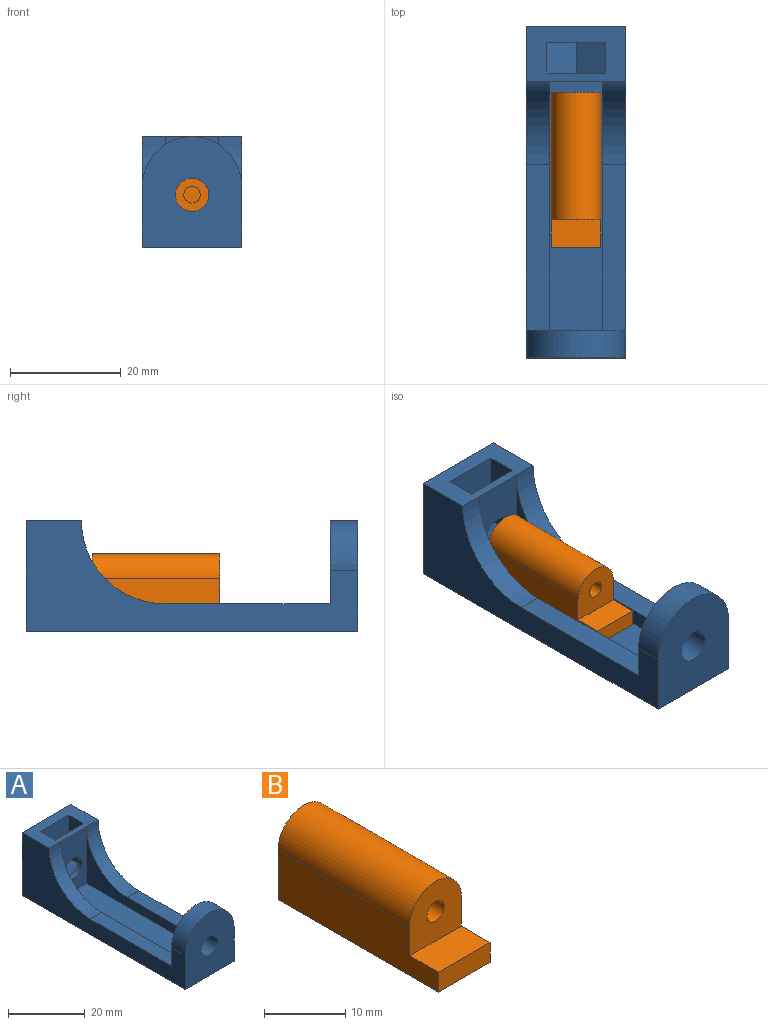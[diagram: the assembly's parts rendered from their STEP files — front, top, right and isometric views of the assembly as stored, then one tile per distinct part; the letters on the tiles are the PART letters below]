
ASSEMBLY  parts=2 mates=1
PART A: 25 faces, bbox 18x60x20 mm
  f0: plane 30x4.25mm, normal (0,0,1), area 127.5mm2, adj f3,f10,f19,f23
  f1: plane 18x10mm, normal (0,0,1), area 122.2mm2, adj f3,f4,f6,f8,f12,f13,f14,f15
  f2: cylinder r=3.25mm len=6.5mm, axis (0,1,0), area 30.6mm2, adj f8,f12
  f3: plane 60x20mm, normal (-1,0,0), area 528.3mm2, adj f0,f1,f4,f5,f7,f10,f22,f23
  f4: plane 20x18mm, normal (0,1,0), area 326.8mm2, adj f1,f3,f6,f7,f11
  f5: plane 20x18mm, normal (0,-1,0), area 297mm2, adj f3,f6,f7,f21,f22
  f6: plane 60x20mm, normal (1,0,0), area 528.3mm2, adj f1,f4,f5,f7,f9,f10,f22,f24
  f7: plane 60x18mm, normal (0,0,-1), area 1080mm2, adj f3,f4,f5,f6
  f8: plane 18x9.5mm, normal (0,-1,0), area 137.8mm2, adj f1,f2,f18,f19,f20
  f9: plane 30x4.25mm, normal (0,0,1), area 127.5mm2, adj f6,f10,f18,f24
  f10: plane 18x18mm, normal (0,1,0), area 235.5mm2, adj f0,f3,f6,f9,f18,f19,f20,f21
  f11: cylinder r=3.25mm len=6.5mm, axis (0,1,0), area 61.3mm2, adj f4,f13
  f12: plane 16.81x10.5mm, normal (0,1,0), area 127.4mm2, adj f1,f2,f14,f15,f16,f17
  f13: plane 16.81x10.5mm, normal (0,-1,0), area 127.4mm2, adj f1,f11,f14,f15,f16,f17
  f14: plane 13.78x5.5mm, normal (1,0,0), area 75.8mm2, adj f1,f12,f13,f17
  f15: plane 13.78x5.5mm, normal (-1,0,0), area 75.8mm2, adj f1,f12,f13,f16
  f16: plane 5.5x5.25mm, normal (-0.5,0,0.87), area 33.3mm2, adj f12,f13,f15,f17
  f17: plane 5.5x5.25mm, normal (0.5,0,0.87), area 33.3mm2, adj f12,f13,f14,f16
  f18: plane 45x18mm, normal (-1,0,0), area 183.3mm2, adj f8,f9,f10,f20,f24
  f19: plane 45x18mm, normal (1,0,0), area 183.3mm2, adj f0,f8,f10,f20,f23
  f20: plane 45x9.5mm, normal (0,0,1), area 427.5mm2, adj f8,f10,f18,f19
  f21: cylinder r=3mm len=6mm, axis (0,-1,0), area 94.2mm2, adj f5,f10
  f22: cylinder r=9mm len=18mm, axis (0,-1,0), area 141.4mm2, adj f3,f5,f6,f10
  f23: cylinder r=15mm len=15mm, axis (1,0,0), area 100.1mm2, adj f0,f1,f3,f19
  f24: cylinder r=15mm len=15mm, axis (1,0,0), area 100.1mm2, adj f1,f6,f9,f18
PART B: 10 faces, bbox 9x28x12 mm
  f0: plane 28x7.5mm, normal (-1,0,0), area 187.5mm2, adj f1,f3,f4,f5,f6,f9
  f1: plane 28x9mm, normal (0,0,-1), area 252mm2, adj f0,f2,f3,f4
  f2: plane 28x7.5mm, normal (1,0,0), area 187.5mm2, adj f1,f3,f4,f5,f6,f9
  f3: plane 12x9mm, normal (0,1,0), area 99.3mm2, adj f0,f1,f2,f9
  f4: plane 9x3mm, normal (0,-1,0), area 27mm2, adj f0,f1,f2,f5
  f5: plane 9x5mm, normal (0,0,1), area 45mm2, adj f0,f2,f4,f6
  f6: plane 9x9mm, normal (0,-1,0), area 65.2mm2, adj f0,f2,f5,f8,f9
  f7: plane 3x3mm, normal (0,-1,0), area 7.1mm2, adj f8
  f8: cylinder r=1.5mm len=20mm, axis (0,-1,0), area 188.5mm2, adj f6,f7
  f9: cylinder r=4.5mm len=23mm, axis (0,-1,0), area 325.2mm2, adj f0,f2,f3,f6
PLACE A t=(2.76,-13.18,3.67)mm
PLACE B t=(2.76,-7.18,5.67)mm
MATE slider A.f20 <-> B.f1  axis (0,0,1) through (2.76,22.82,5.67)mm
